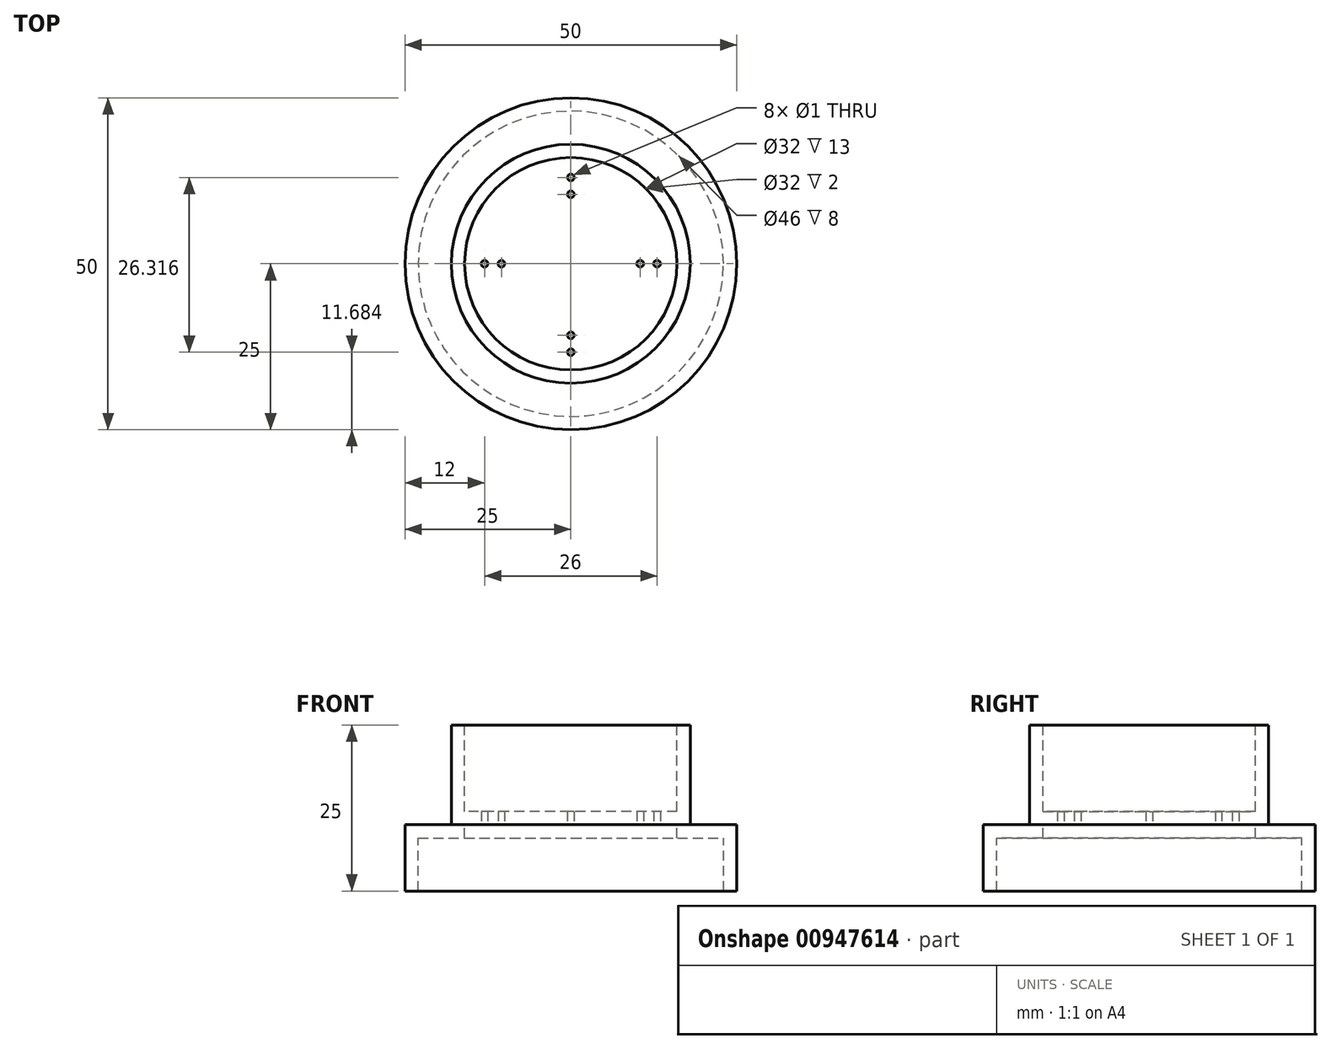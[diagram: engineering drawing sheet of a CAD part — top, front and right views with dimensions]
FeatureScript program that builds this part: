
annotation { "Feature Type Name" : "Feature", "Feature Type Description" : "" }
export const myFeature = defineFeature(function(context is Context, id is Id, definition is map)
    precondition{}
    {
        {
            var Q0;
            Q0=qCreatedBy(makeId("Top.planeOp"),FACE);
            var sketch = newSketch(context, id + "F0", { "sketchPlane" : qUnion([Q0])});
            skCircle(sketch, "E0", {"center": v(0, 0) * mm, "radius": 18 * mm});
            skSolve(sketch);
        }
        {
            var Q0;
            Q0=makeQuery(id+"F0.imprint","IMPRINT",FACE,{"disambiguationData":[TD([[makeQuery(id+"F0.imprint","IMPRINT",EDGE,{"derivedFrom":sQuery(id+"F0.wireOp",EDGE,"E0")}),1.0]])]});
            extrude(context, id + "F1", {"entities" : qUnion([Q0]), "oppositeDirection" : true, "depth" : 15 * mm, "offsetDistance" : 25 * mm});
        }
        {
            var Q0;
            Q0=makeQuery(id+"F1.opExtrude","CAP_FACE",FACE,{"disambiguationData":[OSD([sQuery(id+"F0.wireOp",EDGE,"E0")])],"isStart":true});
            shell(context, id + "F2", {"entities" : qUnion([Q0]), "thickness" : 2 * mm});
        }
        {
            var Q0;
            Q0=makeQuery(id+"F1.opExtrude","CAP_FACE",FACE,{"disambiguationData":[OSD([sQuery(id+"F0.wireOp",EDGE,"E0")])],"isStart":false});
            var sketch = newSketch(context, id + "F3", { "sketchPlane" : qUnion([Q0])});
            skCircle(sketch, "E1", {"center": v(0, 0) * mm, "radius": 25 * mm});
            skSolve(sketch);
        }
        {
            var Q0;
            Q0 = qSketchRegion(id + "F3", true);
            extrude(context, id + "F4", {"entities" : qUnion([Q0]), "operationType" : NewBodyOperationType.ADD, "depth" : 10 * mm, "offsetDistance" : 25 * mm});
        }
        {
            var Q0;
            Q0=makeQuery(id+"F4.opExtrude","CAP_FACE",FACE,{"disambiguationData":[OSD([sQuery(id+"F3.wireOp",EDGE,"E1")])],"isStart":false});
            shell(context, id + "F5", {"entities" : qUnion([Q0]), "thickness" : 2 * mm});
        }
        {
            var Q0;
            {var subQ0=sQuery(id+"F0.wireOp",EDGE,"E0");Q0=makeQuery(id+"F5.opShell","OFFSET_FACE",FACE,{"disambiguationData":[OSD([subQ0]),TDD([makeQuery(id+"F2.opShell","OFFSET_FACE",FACE,{"disambiguationData":[OSD([subQ0]),TDD([makeQuery(id+"F1.opExtrude","CAP_FACE",FACE,{"disambiguationData":[OSD([subQ0])],"isStart":false})])]})])]});}
            var sketch = newSketch(context, id + "F6", { "sketchPlane" : qUnion([Q0])});
            skPoint(sketch, "E2", {"position": v(13, 0) * mm});
            skPoint(sketch, "E3", {"position": v(10.46, 0) * mm});
            skPoint(sketch, "E4", {"position": v(-13, 0) * mm});
            skPoint(sketch, "E5", {"position": v(-10.46, 0) * mm});
            skPoint(sketch, "E6", {"position": v(0, -13) * mm});
            skPoint(sketch, "E7", {"position": v(0, -10.46) * mm});
            skPoint(sketch, "E8", {"position": v(0, 13.32) * mm});
            skPoint(sketch, "E9", {"position": v(0, 10.78) * mm});
            skSolve(sketch);
        }
        {
            var Q0;
            Q0=sQuery(id+"F6.wireOp",VERTEX,"E6");
            var Q1;
            Q1=makeQuery(id+"F1.opExtrude","SWEPT_BODY",BODY,{"disambiguationData":[OSD([sQuery(id+"F0.wireOp",EDGE,"E0")])]});
            hole(context, id + "F7", {"style" : HoleStyle.SIMPLE, "endStyle" : HoleEndStyle.THROUGH, "holeDiameter" : 1 * mm, "majorDiameter" : 5 * mm, "isTappedThrough" : true, "tappedDepth" : 12 * mm, "tapClearance" : 3, "startFromSketch" : true, "locations" : qUnion([Q0]), "scope" : qUnion([Q1])});
        }
        {
            var Q0;
            Q0=sQuery(id+"F6.wireOp",VERTEX,"E7");
            var Q1;
            Q1=makeQuery(id+"F1.opExtrude","SWEPT_BODY",BODY,{"disambiguationData":[OSD([sQuery(id+"F0.wireOp",EDGE,"E0")])]});
            hole(context, id + "F8", {"style" : HoleStyle.SIMPLE, "endStyle" : HoleEndStyle.THROUGH, "holeDiameter" : 1 * mm, "majorDiameter" : 5 * mm, "isTappedThrough" : true, "tappedDepth" : 12 * mm, "tapClearance" : 3, "startFromSketch" : true, "locations" : qUnion([Q0]), "scope" : qUnion([Q1])});
        }
        {
            var Q0;
            Q0=sQuery(id+"F6.wireOp",VERTEX,"E4");
            var Q1;
            Q1=makeQuery(id+"F1.opExtrude","SWEPT_BODY",BODY,{"disambiguationData":[OSD([sQuery(id+"F0.wireOp",EDGE,"E0")])]});
            hole(context, id + "F9", {"style" : HoleStyle.SIMPLE, "endStyle" : HoleEndStyle.THROUGH, "holeDiameter" : 1 * mm, "majorDiameter" : 5 * mm, "isTappedThrough" : true, "tappedDepth" : 12 * mm, "tapClearance" : 3, "startFromSketch" : true, "locations" : qUnion([Q0]), "scope" : qUnion([Q1])});
        }
        {
            var Q0;
            Q0=sQuery(id+"F6.wireOp",VERTEX,"E5");
            var Q1;
            Q1=makeQuery(id+"F1.opExtrude","SWEPT_BODY",BODY,{"disambiguationData":[OSD([sQuery(id+"F0.wireOp",EDGE,"E0")])]});
            hole(context, id + "F10", {"style" : HoleStyle.SIMPLE, "endStyle" : HoleEndStyle.THROUGH, "holeDiameter" : 1 * mm, "majorDiameter" : 5 * mm, "isTappedThrough" : true, "tappedDepth" : 12 * mm, "tapClearance" : 3, "startFromSketch" : true, "locations" : qUnion([Q0]), "scope" : qUnion([Q1])});
        }
        {
            var Q0;
            Q0=sQuery(id+"F6.wireOp",VERTEX,"E8");
            var Q1;
            Q1=makeQuery(id+"F1.opExtrude","SWEPT_BODY",BODY,{"disambiguationData":[OSD([sQuery(id+"F0.wireOp",EDGE,"E0")])]});
            hole(context, id + "F11", {"style" : HoleStyle.SIMPLE, "endStyle" : HoleEndStyle.THROUGH, "holeDiameter" : 1 * mm, "majorDiameter" : 5 * mm, "isTappedThrough" : true, "tappedDepth" : 12 * mm, "tapClearance" : 3, "startFromSketch" : true, "locations" : qUnion([Q0]), "scope" : qUnion([Q1])});
        }
        {
            var Q0;
            Q0=sQuery(id+"F6.wireOp",VERTEX,"E9");
            var Q1;
            Q1=makeQuery(id+"F1.opExtrude","SWEPT_BODY",BODY,{"disambiguationData":[OSD([sQuery(id+"F0.wireOp",EDGE,"E0")])]});
            hole(context, id + "F12", {"style" : HoleStyle.SIMPLE, "endStyle" : HoleEndStyle.THROUGH, "holeDiameter" : 1 * mm, "majorDiameter" : 5 * mm, "isTappedThrough" : true, "tappedDepth" : 12 * mm, "tapClearance" : 3, "startFromSketch" : true, "locations" : qUnion([Q0]), "scope" : qUnion([Q1])});
        }
        {
            var Q0;
            Q0=sQuery(id+"F6.wireOp",VERTEX,"E2");
            var Q1;
            Q1=makeQuery(id+"F1.opExtrude","SWEPT_BODY",BODY,{"disambiguationData":[OSD([sQuery(id+"F0.wireOp",EDGE,"E0")])]});
            hole(context, id + "F13", {"style" : HoleStyle.SIMPLE, "endStyle" : HoleEndStyle.THROUGH, "holeDiameter" : 1 * mm, "majorDiameter" : 5 * mm, "isTappedThrough" : true, "tappedDepth" : 12 * mm, "tapClearance" : 3, "startFromSketch" : true, "locations" : qUnion([Q0]), "scope" : qUnion([Q1])});
        }
        {
            var Q0;
            Q0=sQuery(id+"F6.wireOp",VERTEX,"E3");
            var Q1;
            Q1=makeQuery(id+"F1.opExtrude","SWEPT_BODY",BODY,{"disambiguationData":[OSD([sQuery(id+"F0.wireOp",EDGE,"E0")])]});
            hole(context, id + "F14", {"style" : HoleStyle.SIMPLE, "endStyle" : HoleEndStyle.THROUGH, "holeDiameter" : 1 * mm, "majorDiameter" : 5 * mm, "isTappedThrough" : true, "tappedDepth" : 12 * mm, "tapClearance" : 3, "startFromSketch" : true, "locations" : qUnion([Q0]), "scope" : qUnion([Q1])});
        }
    });
